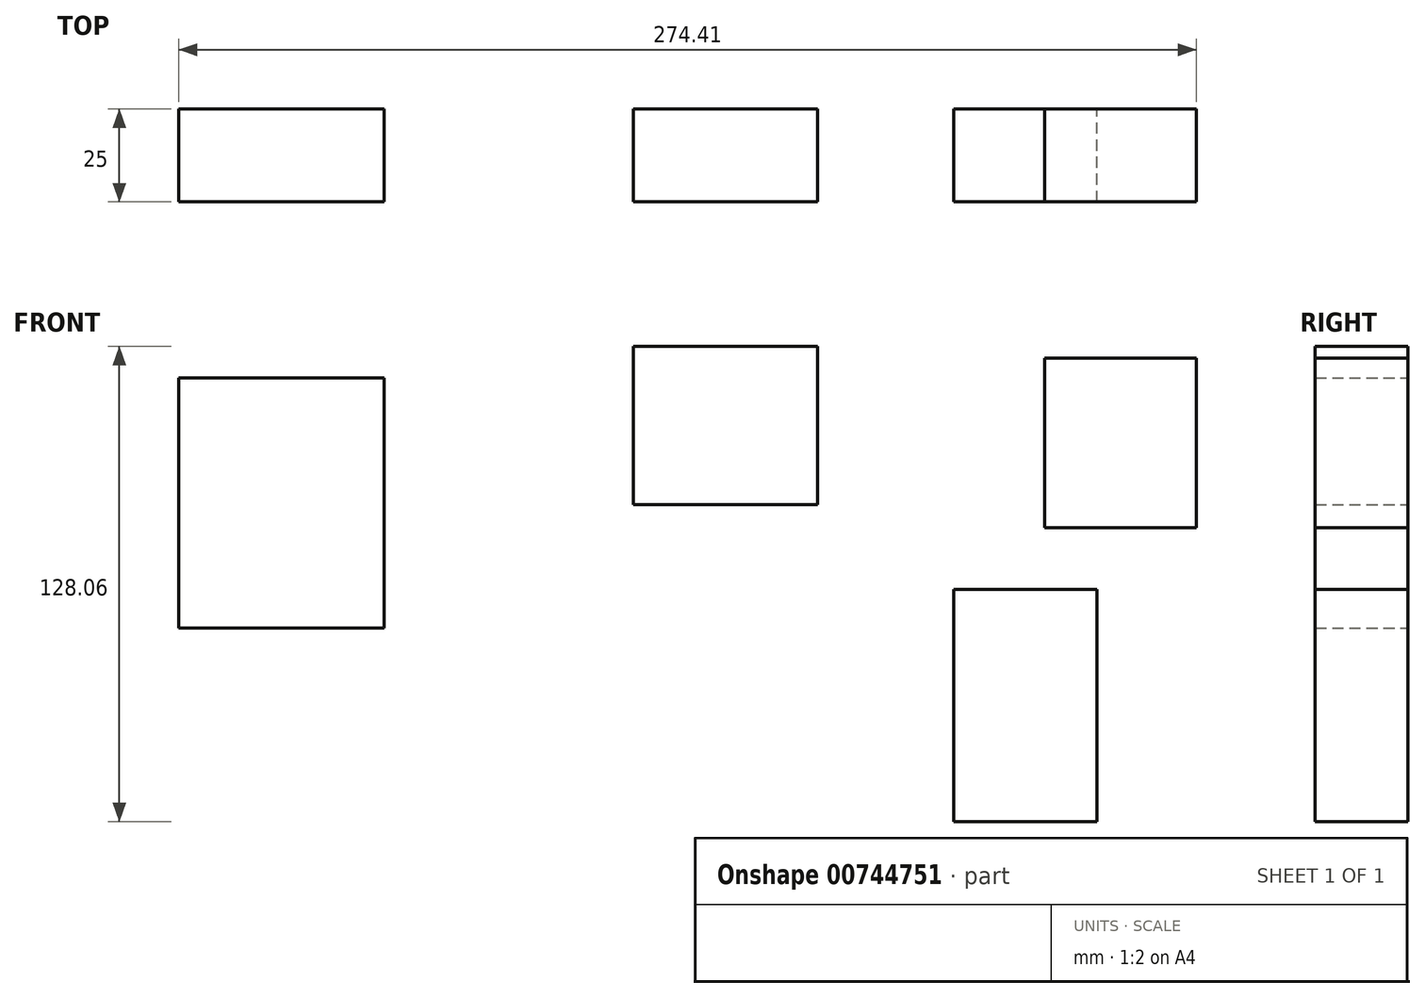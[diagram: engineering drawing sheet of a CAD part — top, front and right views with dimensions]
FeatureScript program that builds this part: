
annotation { "Feature Type Name" : "Feature", "Feature Type Description" : "" }
export const myFeature = defineFeature(function(context is Context, id is Id, definition is map)
    precondition{}
    {
        {
            var Q0;
            Q0=qCreatedBy(makeId("Front.planeOp"),FACE);
            var sketch = newSketch(context, id + "F0", { "sketchPlane" : qUnion([Q0])});
            skLineSegment(sketch, "E0.bottom", {"start": v(-122.6, 10.93) * mm, "end": v(-67.23, 10.93) * mm});
            skLineSegment(sketch, "E0.top", {"start": v(-122.6, 78.32) * mm, "end": v(-67.23, 78.32) * mm});
            skLineSegment(sketch, "E0.left", {"start": v(-122.6, 10.93) * mm, "end": v(-122.6, 78.32) * mm});
            skLineSegment(sketch, "E0.right", {"start": v(-67.23, 10.93) * mm, "end": v(-67.23, 78.32) * mm});
            skPoint(sketch, "E0.middle", {"position": v(-94.91, 44.63) * mm});
            skLineSegment(sketch, "E1.bottom", {"start": v(0, 44.1) * mm, "end": v(49.64, 44.1) * mm});
            skLineSegment(sketch, "E1.top", {"start": v(0, 86.8) * mm, "end": v(49.64, 86.8) * mm});
            skLineSegment(sketch, "E1.left", {"start": v(0, 44.1) * mm, "end": v(0, 86.8) * mm});
            skLineSegment(sketch, "E1.right", {"start": v(49.64, 44.1) * mm, "end": v(49.64, 86.8) * mm});
            skPoint(sketch, "E1.middle", {"position": v(24.82, 65.45) * mm});
            skLineSegment(sketch, "E2.bottom", {"start": v(110.9, 38) * mm, "end": v(151.82, 38) * mm});
            skLineSegment(sketch, "E2.top", {"start": v(110.9, 83.72) * mm, "end": v(151.82, 83.72) * mm});
            skLineSegment(sketch, "E2.left", {"start": v(110.9, 38) * mm, "end": v(110.9, 83.72) * mm});
            skLineSegment(sketch, "E2.right", {"start": v(151.82, 38) * mm, "end": v(151.82, 83.72) * mm});
            skPoint(sketch, "E2.middle", {"position": v(131.36, 60.86) * mm});
            skLineSegment(sketch, "E3.bottom", {"start": v(86.36, -41.26) * mm, "end": v(124.93, -41.26) * mm});
            skLineSegment(sketch, "E3.top", {"start": v(86.36, 21.3) * mm, "end": v(124.93, 21.3) * mm});
            skLineSegment(sketch, "E3.left", {"start": v(86.36, -41.26) * mm, "end": v(86.36, 21.3) * mm});
            skLineSegment(sketch, "E3.right", {"start": v(124.93, -41.26) * mm, "end": v(124.93, 21.3) * mm});
            skPoint(sketch, "E3.middle", {"position": v(105.64, -9.98) * mm});
            skSolve(sketch);
        }
        {
            var Q0;
            Q0 = qSketchRegion(id + "F0", true);
            extrude(context, id + "F1", {"entities" : qUnion([Q0]), "depth" : 25 * mm, "offsetDistance" : 25 * mm});
        }
    });
